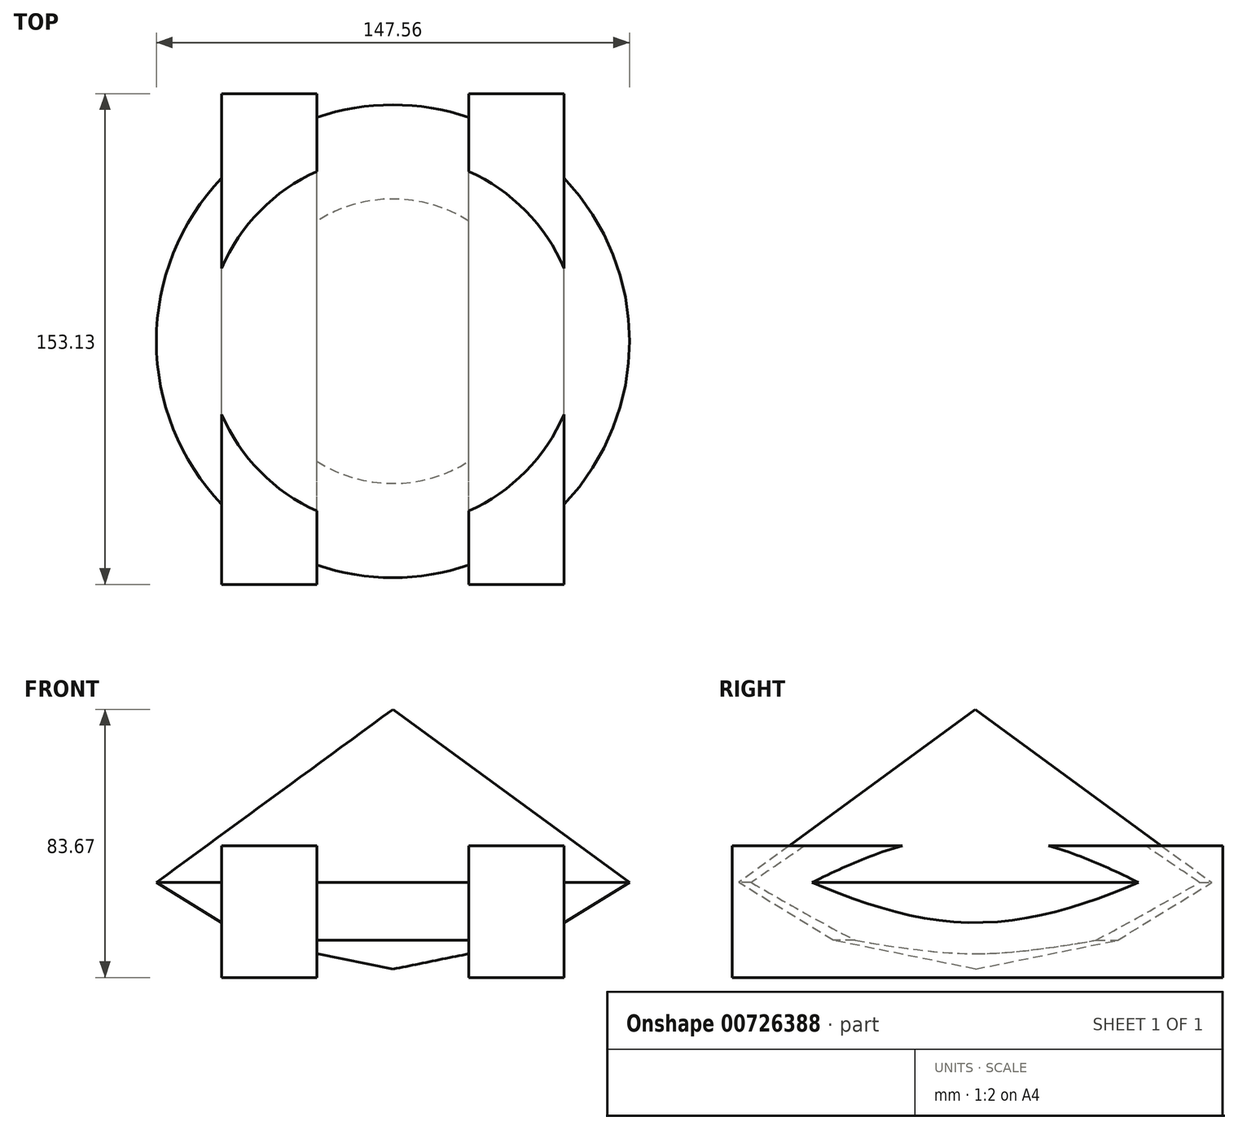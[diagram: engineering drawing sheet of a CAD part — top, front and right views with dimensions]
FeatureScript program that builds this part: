
annotation { "Feature Type Name" : "Feature", "Feature Type Description" : "" }
export const myFeature = defineFeature(function(context is Context, id is Id, definition is map)
    precondition{}
    {
        {
            var Q0;
            Q0=qCreatedBy(makeId("Front.planeOp"),FACE);
            var sketch = newSketch(context, id + "F0", { "sketchPlane" : qUnion([Q0])});
            skLineSegment(sketch, "E0", {"start": v(0, -38.55) * mm, "end": v(44.38, -29.54) * mm});
            skLineSegment(sketch, "E1", {"start": v(44.38, -29.54) * mm, "end": v(73.78, -11.52) * mm});
            skLineSegment(sketch, "E2", {"start": v(73.78, -11.52) * mm, "end": v(0, 42.52) * mm});
            skLineSegment(sketch, "E3", {"start": v(0, 42.52) * mm, "end": v(0, -38.55) * mm});
            skSolve(sketch);
        }
        {
            var Q0;
            Q0=makeQuery(id+"F0.imprint","IMPRINT",FACE,{"disambiguationData":[TD([[makeQuery(id+"F0.imprint","IMPRINT",EDGE,{"derivedFrom":sQuery(id+"F0.wireOp",EDGE,"E0")}),1.0]])]});
            var Q1;
            Q1=sQuery(id+"F0.wireOp",EDGE,"E3");
            revolve(context, id + "F1", {"surfaceOperationType" : NewSurfaceOperationType.NEW, "entities" : qUnion([Q0]), "axis" : qUnion([Q1]), "revolveType" : RevolveType.FULL});
        }
        {
            var Q0;
            Q0=qCreatedBy(makeId("Top.planeOp"),FACE);
            var sketch = newSketch(context, id + "F2", { "sketchPlane" : qUnion([Q0])});
            skLineSegment(sketch, "E4.bottom", {"start": v(-23.71, -75.9) * mm, "end": v(-53.38, -75.9) * mm});
            skLineSegment(sketch, "E4.top", {"start": v(-23.71, 77.23) * mm, "end": v(-53.38, 77.23) * mm});
            skLineSegment(sketch, "E4.left", {"start": v(-23.71, -75.9) * mm, "end": v(-23.71, 77.23) * mm});
            skLineSegment(sketch, "E4.right", {"start": v(-53.38, -75.9) * mm, "end": v(-53.38, 77.23) * mm});
            skLineSegment(sketch, "E5.MirrorCS", {"start": v(23.71, -75.9) * mm, "end": v(23.71, 77.23) * mm});
            skLineSegment(sketch, "E6.MirrorCS", {"start": v(53.38, -75.9) * mm, "end": v(53.38, 77.23) * mm});
            skLineSegment(sketch, "E7.MirrorCS", {"start": v(23.71, 77.23) * mm, "end": v(53.38, 77.23) * mm});
            skLineSegment(sketch, "E8.MirrorCS", {"start": v(23.71, -75.9) * mm, "end": v(53.38, -75.9) * mm});
            skSolve(sketch);
        }
        {
            var Q0;
            Q0=makeQuery(id+"F2.imprint","IMPRINT",FACE,{"disambiguationData":[TD([[makeQuery(id+"F2.imprint","IMPRINT",EDGE,{"derivedFrom":sQuery(id+"F2.wireOp",EDGE,"E4.bottom")}),-1.0]])]});
            var Q1;
            Q1=makeQuery(id+"F2.imprint","IMPRINT",FACE,{"disambiguationData":[TD([[makeQuery(id+"F2.imprint","IMPRINT",EDGE,{"derivedFrom":sQuery(id+"F2.wireOp",EDGE,"E5.MirrorCS")}),-1.0]])]});
            extrude(context, id + "F3", {"entities" : qUnion([Q0, Q1]), "operationType" : NewBodyOperationType.ADD, "oppositeDirection" : true, "depth" : 41.15 * mm, "offsetDistance" : 25.4 * mm});
        }
        {
            var Q0;
            Q0=makeQuery(id+"F3.opExtrude","SWEPT_FACE",FACE,{"disambiguationData":[OSD([sQuery(id+"F2.wireOp",EDGE,"E6.MirrorCS")])]});
            var sketch = newSketch(context, id + "F4", { "sketchPlane" : qUnion([Q0])});
            skCircle(sketch, "E9", {"center": v(-71.82, -36.12) * mm, "radius": 14.58 * mm});
            skCircle(sketch, "E10.1.0.0", {"center": v(-35.75, -36.12) * mm, "radius": 14.58 * mm});
            skCircle(sketch, "E10.2.0.0", {"center": v(0.32, -36.12) * mm, "radius": 14.58 * mm});
            skCircle(sketch, "E10.3.0.0", {"center": v(36.39, -36.12) * mm, "radius": 14.58 * mm});
            skCircle(sketch, "E10.4.0.0", {"center": v(72.46, -36.12) * mm, "radius": 14.58 * mm});
            skLineSegment(sketch, "E10.direction1", {"start": v(-71.82, -36.12) * mm, "end": v(-35.75, -36.12) * mm, "construction": true});
            skSolve(sketch);
        }
        {
            var Q0;
            Q0=sQuery(id+"F4.wireOp",EDGE,"E9");
            var Q1;
            Q1=sQuery(id+"F4.wireOp",EDGE,"E10.1.0.0");
            var Q2;
            Q2=sQuery(id+"F4.wireOp",EDGE,"E10.2.0.0");
            var Q3;
            Q3=sQuery(id+"F4.wireOp",EDGE,"E10.3.0.0");
            var Q4;
            Q4=sQuery(id+"F4.wireOp",EDGE,"E10.4.0.0");
            extrude(context, id + "F5", {"bodyType" : ToolBodyType.SURFACE, "surfaceEntities" : qUnion([Q0, Q1, Q2, Q3, Q4]), "depth" : 25.4 * mm, "offsetDistance" : 25.4 * mm});
        }
    });
